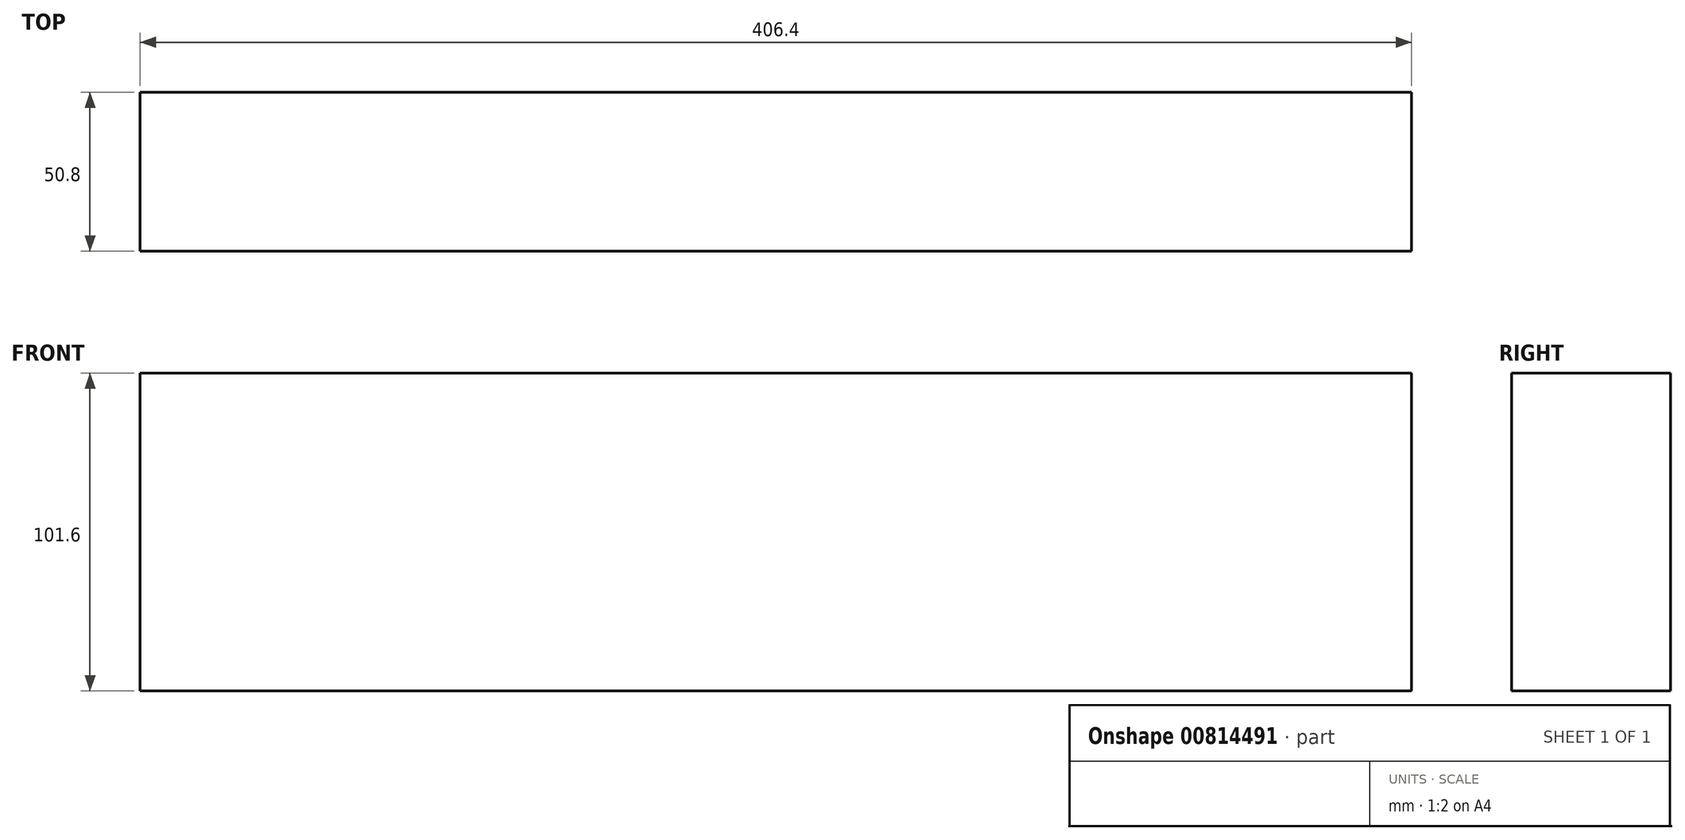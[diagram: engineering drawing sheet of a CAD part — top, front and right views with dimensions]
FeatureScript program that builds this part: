
annotation { "Feature Type Name" : "Feature", "Feature Type Description" : "" }
export const myFeature = defineFeature(function(context is Context, id is Id, definition is map)
    precondition{}
    {
        {
            var Q0;
            Q0=qCreatedBy(makeId("Front.planeOp"),FACE);
            var sketch = newSketch(context, id + "F0", { "sketchPlane" : qUnion([Q0])});
            skLineSegment(sketch, "E0.bottom", {"start": v(0, 0) * mm, "end": v(406.4, 0) * mm});
            skLineSegment(sketch, "E0.top", {"start": v(0, 101.6) * mm, "end": v(406.4, 101.6) * mm});
            skLineSegment(sketch, "E0.left", {"start": v(0, 0) * mm, "end": v(0, 101.6) * mm});
            skLineSegment(sketch, "E0.right", {"start": v(406.4, 0) * mm, "end": v(406.4, 101.6) * mm});
            skSolve(sketch);
        }
        {
            var Q0;
            Q0 = qSketchRegion(id + "F0", true);
            extrude(context, id + "F1", {"entities" : qUnion([Q0]), "depth" : 50.8 * mm, "offsetDistance" : 25.4 * mm});
        }
    });
